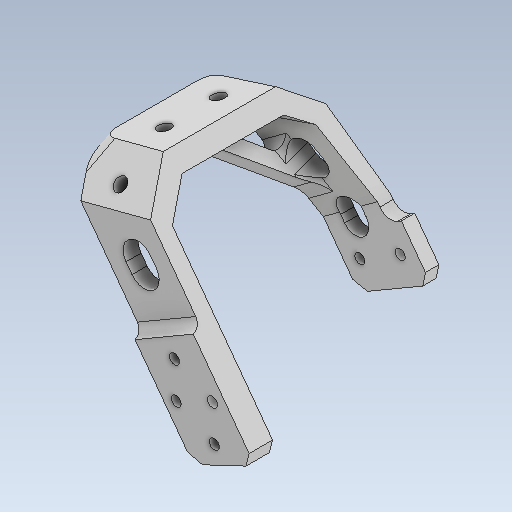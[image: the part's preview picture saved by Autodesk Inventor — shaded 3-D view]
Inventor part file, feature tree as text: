
AUTODESK INVENTOR PART (.ipt)
format: ipt  version: 2020 (Build 240168000, 168)  size: 516,096 bytes
history: native  units: mm
features: sketch x18, extrude x18, projected_geometry x15, reference x12, chamfer x7, fillet x6, other x5, thicken_offset x2, plane x1
ambient origin geometry x8: Origin, YZ Plane, XZ Plane, XY Plane, X Axis, Y Axis, Z Axis, Center Point
bodies: Solid1 (feature_tree)
feature tree (84):
  sketch  "Sketch1"  dims[d0=20.0mm d1=10.0mm d2=0.0mm]
  plane  "Work Plane1"
  extrude  "Extrusion1"  Depth=10.0mm TaperAngle=0.0deg
  extrude  "Extrusion2"  Depth=20.0mm
  extrude  "Extrusion3"  Depth=10.0mm
  extrude  "Extrusion4"  Depth=4.0mm
  extrude  "Extrusion5"  Depth=20.0mm
  thicken_offset  "Thicken1"
  extrude  "Extrusion6"  Depth=10.0mm TaperAngle=0.0deg
  extrude  "Extrusion7"  Depth=10.0mm TaperAngle=0.0deg
  fillet  "Fillet1"  Radius=100.0mm
  extrude  "Extrusion8"  Depth=10.0mm
  fillet  "Fillet2"  Radius=10.0mm
  fillet  "Fillet3"  Radius=5.0mm
  fillet  "Fillet5"  Radius=10.0mm
  chamfer  "Chamfer2"  Distance=6.0mm
  chamfer  "Chamfer3"  Distance=5.0mm Angle=45.0deg
  chamfer  "Chamfer4"  Distance=8.0mm Angle=45.0deg
  chamfer  "Chamfer5"  Distance=8.0mm Angle=45.0deg
  extrude  "Extrusion9"  Depth=8.0mm
  extrude  "Extrusion10"  Depth=4.0mm
  extrude  "Extrusion11"  Depth=4.0mm
  chamfer  "Chamfer6"  Distance=12.0mm
  fillet  "Fillet7"  Radius=4.0mm
  extrude  "Extrusion12"  Depth=8.0mm TaperAngle=0.0deg
  chamfer  "Chamfer7"  Distance=4.0mm
  extrude  "Extrusion13"  Depth=8.0mm TaperAngle=0.0deg
  chamfer  "Chamfer8"  Distance=3.0mm Angle=45.0deg
  extrude  "Extrusion14"  Depth=5.0mm
  extrude  "Extrusion15"  Depth=8.0mm
  fillet  "Fillet8"  Radius=7.0mm
  extrude  "Extrusion16"  Depth=3.0mm
  thicken_offset  "Thicken2"
  extrude  "Extrusion17"  Depth=3.0mm
  extrude  "Extrusion18"  Depth=8.0mm TaperAngle=0.0deg
  reference  "Reference1"
  sketch  "Sketch2"  dims[d3=10.0mm d4=20.0mm]
  projected_geometry  "Projected Loop1"
  sketch  "Sketch3"  dims[d5=10.0mm d6=0.0mm d7=26.0mm]
  projected_geometry  "Projected Loop2"
  reference  "Reference4"
  reference  "Reference5"
  sketch  "Sketch4"  dims[d9=31.0mm d11=4.0mm]
  projected_geometry  "Projected Loop3"
  sketch  "Sketch5"  dims[d12=20.0mm d13=53.0mm]
  sketch  "Sketch6"  dims[d14=41.0mm d15=10.0mm d16=0.0mm]
  reference  "Reference6"
  projected_geometry  "Projected Loop4"
  sketch  "Sketch7"  dims[d17=8.0mm d18=10.0mm d19=0.0mm d20=100.0mm d21=0.0mm]
  reference  "Reference7"
  projected_geometry  "Projected Loop5"
  sketch  "Sketch8"  dims[d22=1.0mm d23=1.0mm d24=10.0mm d25=0.0mm d26=5.0mm d27=10.0mm d28=0.0mm]
  projected_geometry  "Projected Loop6"
  sketch  "Sketch9"  dims[d29=4.0mm]
  projected_geometry  "Projected Loop7"
  sketch  "Sketch10"  dims[d30=28.0mm]
  projected_geometry  "Projected Loop8"
  sketch  "Sketch11"  dims[d31=22.0mm]
  projected_geometry  "Projected Loop9"
  sketch  "Sketch12"  dims[d32=6.0mm]
  projected_geometry  "Projected Loop10"
  sketch  "Sketch13"  dims[d33=7.0mm d34=6.0mm d35=0.0mm]
  reference  "Reference8"
  reference  "Reference9"
  sketch  "Sketch14"  dims[d36=2.0mm]
  projected_geometry  "Projected Loop11"
  reference  "Reference10"
  reference  "Reference11"
  reference  "Reference12"
  reference  "Reference13"
  sketch  "Sketch15"  dims[d37=3.0mm]
  projected_geometry  "Projected Loop12"
  reference  "Reference14"
  sketch  "Sketch16"  dims[d39=8.0mm d44=5.0mm d45=2.0mm d46=45.0deg d47=8.0mm d48=2.0mm d49=45.0deg d50=8.0mm d51=2.0mm d52=45.0deg]
  projected_geometry  "Projected Loop13"
  sketch  "Sketch17"  dims[d53=13.0mm d54=2.0mm d55=45.0deg d56=8.0mm]
  projected_geometry  "Projected Loop14"
  sketch  "Sketch18"  dims[d57=8.0mm d58=4.0mm d59=4.0mm d60=12.0mm d61=0.0mm d62=4.0mm d63=7.0mm d64=0.0mm d65=4.0mm d66=7.0mm d67=0.0mm d68=3.0mm d69=2.0mm d70=45.0deg d71=5.0mm d72=7.0mm d73=7.0mm d74=3.0mm d75=3.0mm d76=7.0mm d77=0.0mm d78=3.0mm d79=2.0mm d80=45.0deg d81=6.0mm d82=6.0mm d83=3.0mm d84=3.0mm d85=7.0mm d86=0.0mm d87=3.0mm d88=2.0mm d89=45.0deg d90=10.0mm d91=10.0mm d92=3.0mm d93=3.0mm d94=7.0mm d95=0.0mm d96=2.5mm d97=0.0mm d98=3.0mm d99=1.5mm d100=8.0mm d101=5.0mm d102=0.0mm d103=0.5mm d104=0.5mm d105=7.0mm d106=1.5mm d107=8.0mm d108=8.0mm d109=0.0mm d110=15.0mm d111=1.0mm d112=8.0mm d113=8.0mm d114=0.0mm]
  projected_geometry  "Projected Loop15"
  parser-record x1  (decoder bookkeeping rows leaked as tree rows — omitted from the tree; the rows remain in map.json)
  other  "reducer_1.iam"
  other  "motor_holder_5:1"
  other  "motor_holder_3:1"
  other  "motor_holder_1:1"
note: 1 file-system path scrubbed to <path> (originals preserved in map.json)
